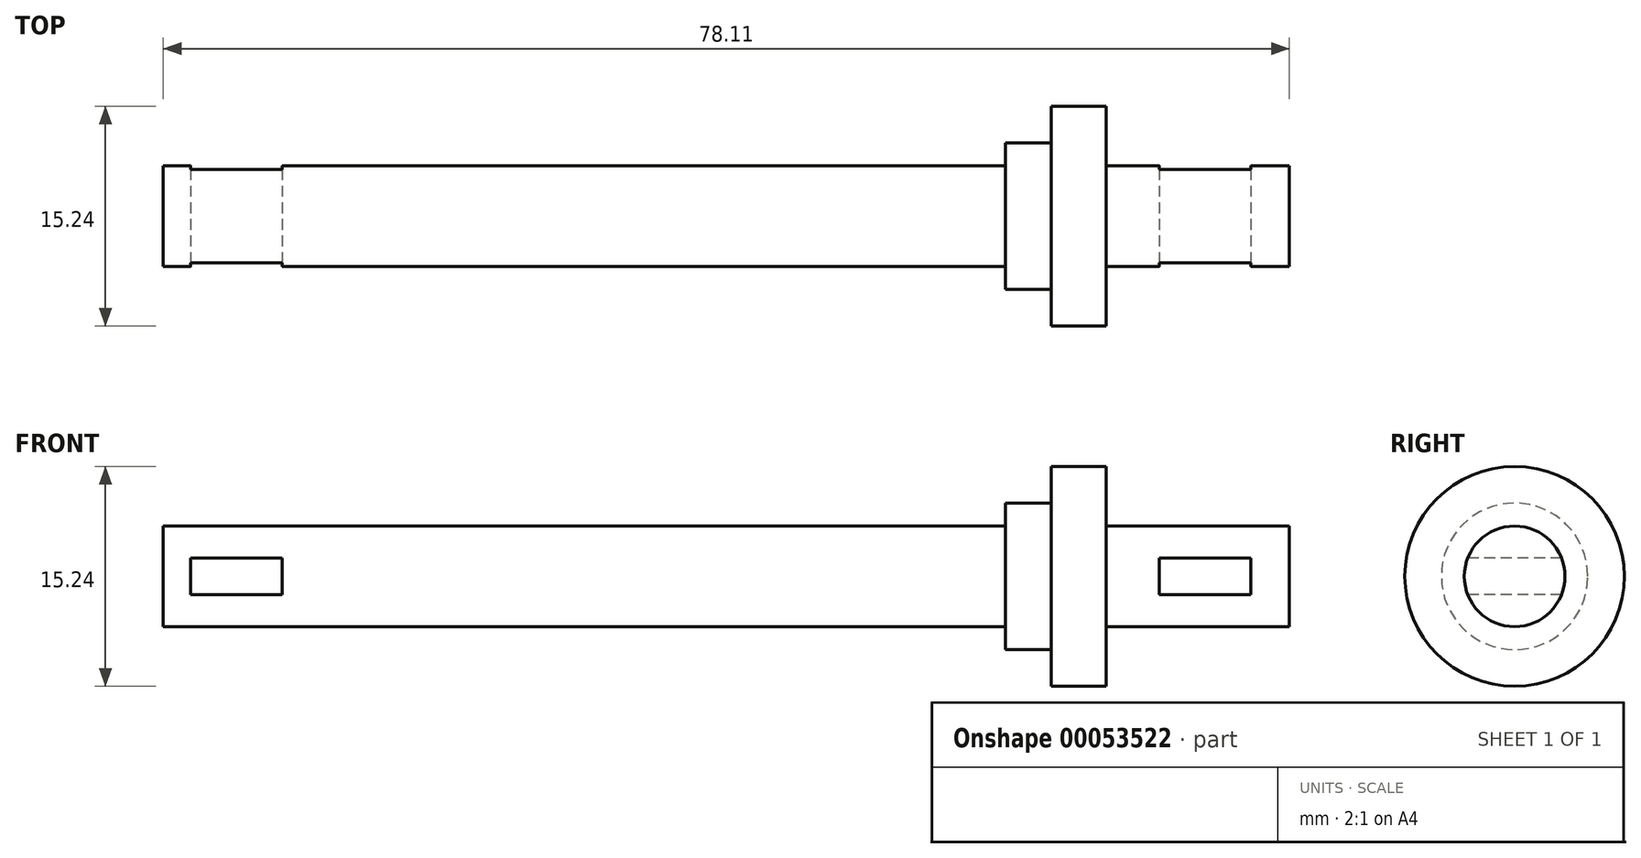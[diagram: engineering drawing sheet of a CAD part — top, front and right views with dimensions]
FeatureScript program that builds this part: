
annotation { "Feature Type Name" : "Feature", "Feature Type Description" : "" }
export const myFeature = defineFeature(function(context is Context, id is Id, definition is map)
    precondition{}
    {
        {
            var Q0;
            Q0=qCreatedBy(makeId("Front.planeOp"),FACE);
            var sketch = newSketch(context, id + "F0", { "sketchPlane" : qUnion([Q0])});
            skLineSegment(sketch, "E0.rect.bottom", {"start": v(29.21, -1.75) * mm, "end": v(-29.21, -1.75) * mm});
            skLineSegment(sketch, "E0.rect.top", {"start": v(29.21, 1.75) * mm, "end": v(-29.21, 1.75) * mm});
            skLineSegment(sketch, "E0.rect.left", {"start": v(29.21, -1.75) * mm, "end": v(29.21, 1.75) * mm});
            skLineSegment(sketch, "E0.rect.right", {"start": v(-29.21, -1.75) * mm, "end": v(-29.21, 1.75) * mm});
            skPoint(sketch, "E0.rect.middle", {"position": v(0, 0) * mm});
            skLineSegment(sketch, "E1.bottom", {"start": v(29.21, -1.75) * mm, "end": v(32.38, -1.75) * mm});
            skLineSegment(sketch, "E1.top", {"start": v(29.21, 3.33) * mm, "end": v(32.38, 3.33) * mm});
            skLineSegment(sketch, "E1.left", {"start": v(29.21, -1.75) * mm, "end": v(29.21, 3.33) * mm});
            skLineSegment(sketch, "E1.right", {"start": v(32.38, -1.75) * mm, "end": v(32.38, 3.33) * mm});
            skLineSegment(sketch, "E2.bottom", {"start": v(32.38, -1.75) * mm, "end": v(36.2, -1.75) * mm});
            skLineSegment(sketch, "E2.top", {"start": v(32.38, 5.87) * mm, "end": v(36.2, 5.87) * mm});
            skLineSegment(sketch, "E2.left", {"start": v(32.38, -1.75) * mm, "end": v(32.38, 5.87) * mm});
            skLineSegment(sketch, "E2.right", {"start": v(36.2, -1.75) * mm, "end": v(36.2, 5.87) * mm});
            skLineSegment(sketch, "E3.bottom", {"start": v(36.2, -1.75) * mm, "end": v(48.9, -1.75) * mm});
            skLineSegment(sketch, "E3.top", {"start": v(36.2, 1.75) * mm, "end": v(48.9, 1.75) * mm});
            skLineSegment(sketch, "E3.left", {"start": v(36.2, -1.75) * mm, "end": v(36.2, 1.75) * mm});
            skLineSegment(sketch, "E3.right", {"start": v(48.9, -1.75) * mm, "end": v(48.9, 1.75) * mm});
            skSolve(sketch);
        }
        {
            var Q0;
            Q0 = qSketchRegion(id + "F0", true);
            var Q1;
            Q1=sQuery(id+"F0.wireOp",EDGE,"E0.rect.bottom");
            revolve(context, id + "F1", {"entities" : qUnion([Q0]), "axis" : qUnion([Q1]), "revolveType" : RevolveType.FULL});
        }
        {
            var Q0;
            Q0=qCreatedBy(makeId("Front.planeOp"),FACE);
            var sketch = newSketch(context, id + "F2", { "sketchPlane" : qUnion([Q0])});
            skLineSegment(sketch, "E4.0", {"start": v(-29.21, 1.75) * mm, "end": v(-29.21, -5.24) * mm});
            skLineSegment(sketch, "E4.1", {"start": v(36.2, 5.87) * mm, "end": v(36.2, -9.37) * mm, "construction": true});
            skLineSegment(sketch, "E5.0", {"start": v(29.21, 3.33) * mm, "end": v(29.21, -6.83) * mm, "construction": true});
            skLineSegment(sketch, "E6", {"start": v(-29.21, -1.75) * mm, "end": v(-15.03, -1.75) * mm, "construction": true});
            skLineSegment(sketch, "E7.1", {"start": v(48.9, 1.75) * mm, "end": v(48.9, -5.24) * mm, "construction": true});
            skLineSegment(sketch, "E7.2", {"start": v(36.2, 1.75) * mm, "end": v(48.9, 1.75) * mm, "construction": true});
            skLineSegment(sketch, "E8.rect.bottom", {"start": v(46.23, -3.02) * mm, "end": v(39.88, -3.02) * mm});
            skLineSegment(sketch, "E8.rect.top", {"start": v(46.23, -0.48) * mm, "end": v(39.88, -0.48) * mm});
            skLineSegment(sketch, "E8.rect.left", {"start": v(46.23, -3.02) * mm, "end": v(46.23, -0.48) * mm});
            skLineSegment(sketch, "E8.rect.right", {"start": v(39.88, -3.02) * mm, "end": v(39.88, -0.48) * mm});
            skPoint(sketch, "E8.rect.middle", {"position": v(43.05, -1.75) * mm});
            skPoint(sketch, "E8.rect.middle.positionSnap0", {"position": v(36.2, -1.75) * mm});
            skPoint(sketch, "E8.rect.centerSnap0", {"position": v(36.2, -1.75) * mm});
            skLineSegment(sketch, "E9.rect.bottom", {"start": v(-20.95, -3.02) * mm, "end": v(-27.3, -3.02) * mm});
            skLineSegment(sketch, "E9.rect.top", {"start": v(-20.95, -0.48) * mm, "end": v(-27.3, -0.48) * mm});
            skLineSegment(sketch, "E9.rect.left", {"start": v(-20.95, -3.02) * mm, "end": v(-20.95, -0.48) * mm});
            skLineSegment(sketch, "E9.rect.right", {"start": v(-27.3, -3.02) * mm, "end": v(-27.3, -0.48) * mm});
            skPoint(sketch, "E9.rect.middle", {"position": v(-24.13, -1.75) * mm});
            skSolve(sketch);
        }
        {
            var Q0;
            Q0=makeQuery(id+"F2.imprint","IMPRINT",FACE,{"disambiguationData":[TD([[makeQuery(id+"F2.imprint","IMPRINT",EDGE,{"derivedFrom":sQuery(id+"F2.wireOp",EDGE,"E9.rect.bottom")}),-1.0]])]});
            var Q1;
            Q1=makeQuery(id+"F2.imprint","IMPRINT",FACE,{"disambiguationData":[TD([[makeQuery(id+"F2.imprint","IMPRINT",EDGE,{"derivedFrom":sQuery(id+"F2.wireOp",EDGE,"E8.rect.bottom")}),-1.0]])]});
            extrude(context, id + "F3", {"entities" : qUnion([Q0, Q1]), "operationType" : NewBodyOperationType.REMOVE, "endBound" : BoundingType.SYMMETRIC, "oppositeDirection" : true, "depth" : 25.4 * mm});
        }
    });
